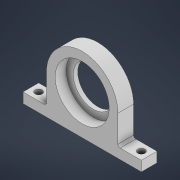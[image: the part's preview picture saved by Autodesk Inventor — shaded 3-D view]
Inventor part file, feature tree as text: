
AUTODESK INVENTOR PART (.ipt)
format: ipt  version: 2021 (Build 250183000, 183)  size: 313,856 bytes
history: native  units: mm
features: extrude x6, sketch x6, fillet x2
ambient origin geometry x8: Origin, YZ Plane, XZ Plane, XY Plane, X Axis, Y Axis, Z Axis, Center Point
bodies: Volumenkörper1 (feature_tree)
feature tree (14):
  extrude  "Extrusion1"  Depth=32.0mm
  sketch  "Skizze2"  dims[d2=24.2mm d3=7.0mm d4=0.0mm]
  extrude  "Extrusion2"  Depth=7.0mm TaperAngle=0.0deg
  extrude  "Extrusion3"  Depth=3.0mm
  extrude  "Extrusion4"  Depth=10.5mm TaperAngle=0.0deg
  fillet  "Rundung1"  Radius=24.2mm
  extrude  "Extrusion5"  Depth=2.0mm TaperAngle=0.0deg
  fillet  "Rundung2"  Radius=16.0mm
  extrude  "Extrusion6"  Depth=1.0mm
  sketch  "Skizze1"  dims[d0=32.0mm d1=32.0mm]
  sketch  "Skizze3"  dims[d5=3.0mm d6=3.0mm]
  sketch  "Skizze4"  dims[d7=10.5mm d8=0.0mm d9=10.5mm d10=0.0mm d11=24.2mm]
  sketch  "Skizze5"  dims[d12=18.0mm d13=2.0mm d14=0.0mm d15=16.0mm]
  sketch  "Skizze6"  dims[d16=3.2mm d17=3.5mm d18=3.5mm d19=3.2mm d20=3.5mm d21=3.5mm d22=5.0mm d23=0.0mm d24=1.0mm d25=3.2mm d26=3.2mm d27=1.5mm d28=0.0mm]
